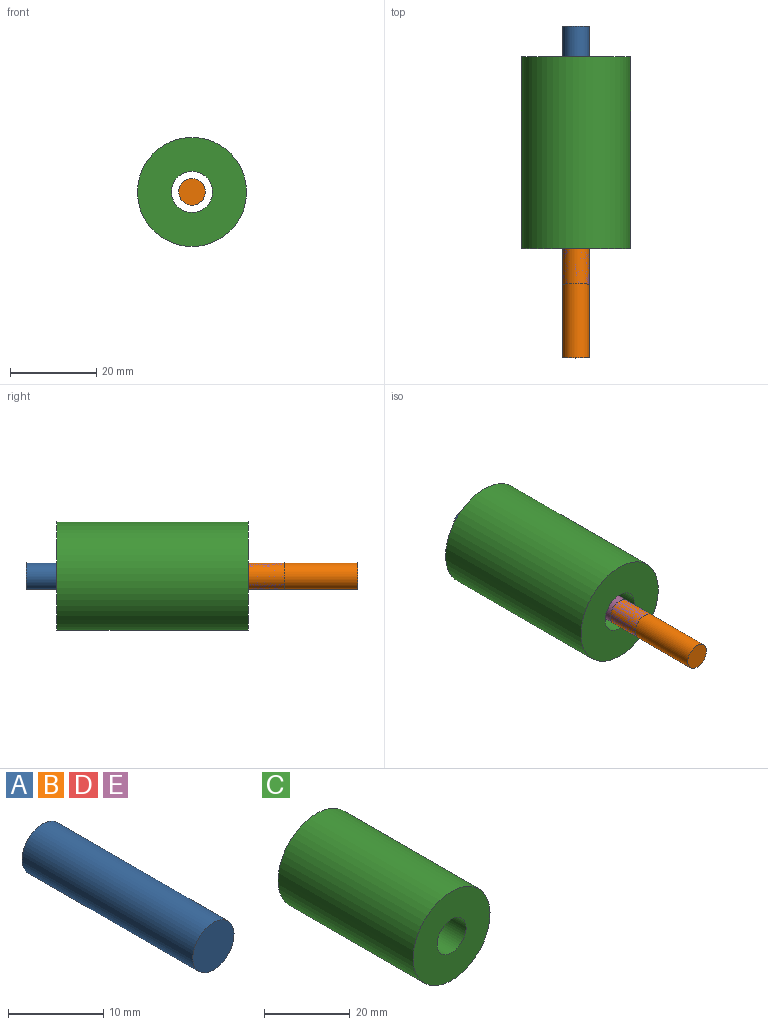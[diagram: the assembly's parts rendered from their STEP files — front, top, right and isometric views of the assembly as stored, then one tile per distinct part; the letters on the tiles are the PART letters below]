
ASSEMBLY  parts=5 mates=4
PART A: 3 faces, bbox 6.1x25.4x6.1 mm
  f0: cylinder r=3.06mm len=25.4mm, axis (0,1,0), area 488.7mm2, adj f1,f2
  f1: plane 6.12x6.12mm, normal (0,-1,0), area 29.5mm2, adj f0
  f2: plane 6.12x6.12mm, normal (0,1,0), area 29.5mm2, adj f0
PART B: same geometry as A
PART C: 4 faces, bbox 25.3x44.5x25.3 mm
  f0: cylinder r=12.65mm len=44.45mm, axis (0,1,0), area 3532.8mm2, adj f1,f2
  f1: plane 25.3x25.3mm, normal (0,-1,0), area 431.1mm2, adj f0,f3
  f2: plane 25.3x25.3mm, normal (0,1,0), area 431.1mm2, adj f0,f3
  f3: cylinder r=4.77mm len=44.45mm, axis (0,-1,0), area 1333.3mm2, adj f1,f2
PART D: same geometry as A
PART E: same geometry as A
PLACE A t=(-15.17,2.29,-16.95)mm fixed
PLACE B t=(-15.17,-49.31,-16.95)mm
PLACE C t=(-24.68,-4.86,-4.38)mm fixed
PLACE D rot(axis=(0,1,0),90deg) t=(-125.35,-4.86,-36.15)mm
PLACE E t=(-15.17,-32.15,-16.95)mm fixed
MATE fastened D.f0 <-> C.f0  axis (0,1,0) through (-79.86,-4.86,28.54)mm
MATE slider C.f0 <-> A.f0  axis (0,1,0) through (-79.86,-4.86,28.54)mm
MATE fastened C.f0 <-> B.f0  axis (0,-1,0) through (-79.86,-49.31,28.54)mm
MATE slider C.f0 <-> E.f0  axis (0,-1,0) through (-79.86,-49.31,28.54)mm
